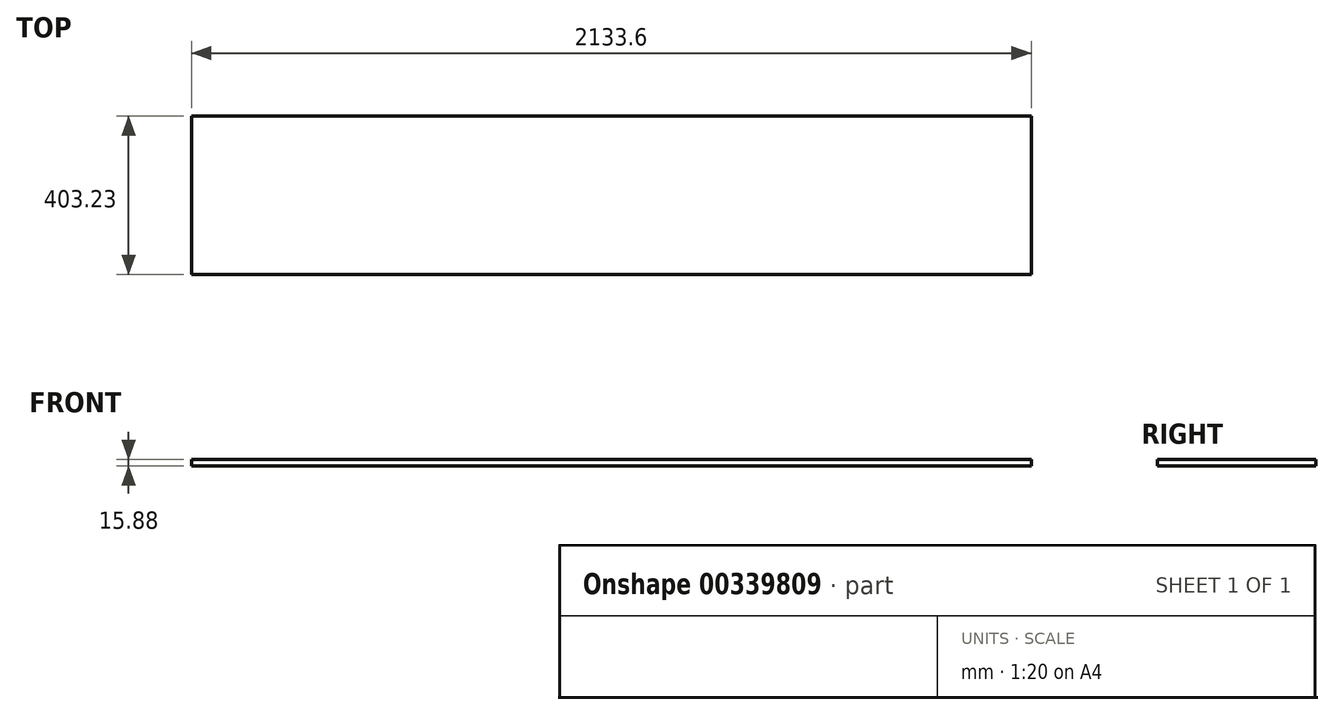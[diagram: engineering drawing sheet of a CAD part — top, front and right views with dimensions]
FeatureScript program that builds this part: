
annotation { "Feature Type Name" : "Feature", "Feature Type Description" : "" }
export const myFeature = defineFeature(function(context is Context, id is Id, definition is map)
    precondition{}
    {
        {
            var Q0;
            Q0=qCreatedBy(makeId("Top.planeOp"),FACE);
            var sketch = newSketch(context, id + "F0", { "sketchPlane" : qUnion([Q0])});
            skLineSegment(sketch, "E0.bottom", {"start": v(-411.7, -152.92) * mm, "end": v(1721.9, -152.92) * mm});
            skLineSegment(sketch, "E0.top", {"start": v(-411.7, 250.3) * mm, "end": v(1721.9, 250.3) * mm});
            skLineSegment(sketch, "E0.left", {"start": v(-411.7, -152.92) * mm, "end": v(-411.7, 250.3) * mm});
            skLineSegment(sketch, "E0.right", {"start": v(1721.9, -152.92) * mm, "end": v(1721.9, 250.3) * mm});
            skSolve(sketch);
        }
        {
            var Q0;
            Q0 = qSketchRegion(id + "F0", true);
            extrude(context, id + "F1", {"entities" : qUnion([Q0]), "oppositeDirection" : true, "depth" : 15.88 * mm});
        }
    });
